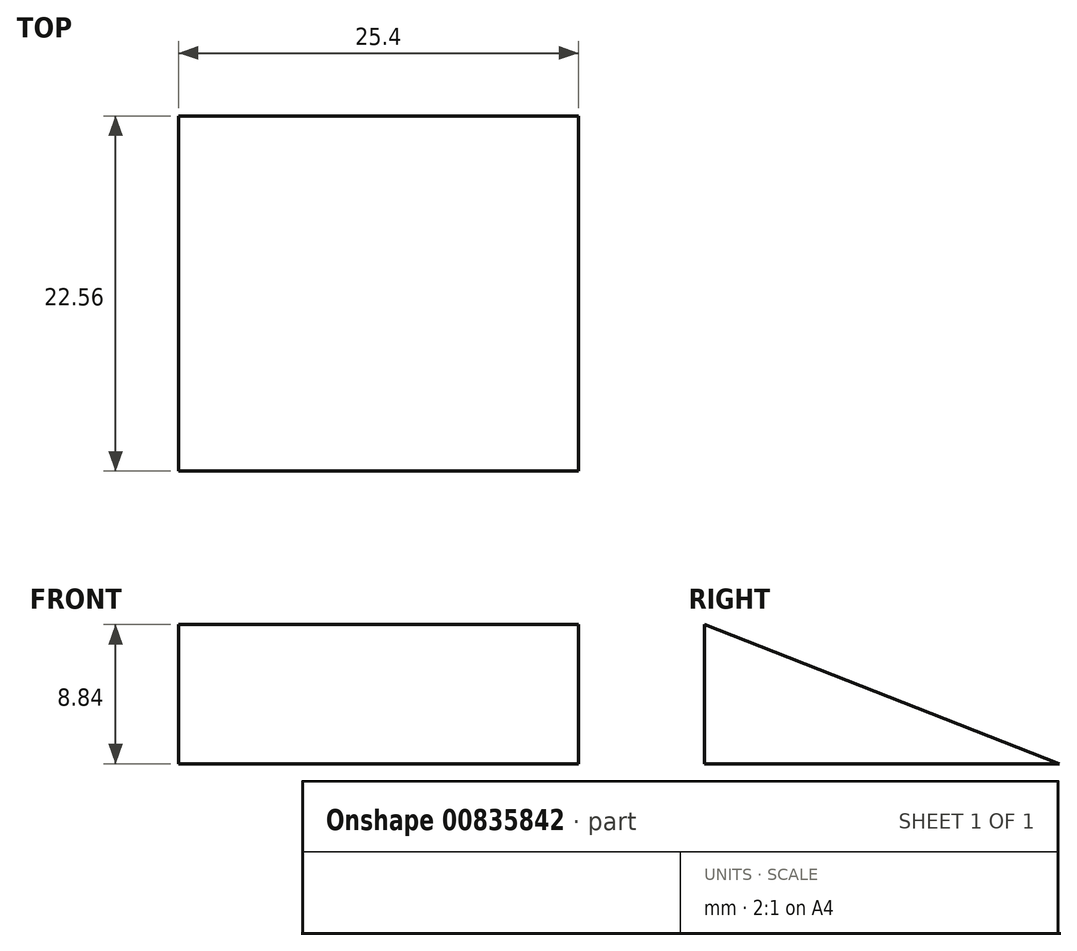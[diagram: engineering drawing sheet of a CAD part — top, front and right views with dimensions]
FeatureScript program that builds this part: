
annotation { "Feature Type Name" : "Feature", "Feature Type Description" : "" }
export const myFeature = defineFeature(function(context is Context, id is Id, definition is map)
    precondition{}
    {
        {
            var Q0;
            Q0=qCreatedBy(makeId("Right.planeOp"),FACE);
            var sketch = newSketch(context, id + "F0", { "sketchPlane" : qUnion([Q0])});
            skLineSegment(sketch, "E0", {"start": v(0, 0) * mm, "end": v(22.56, 0) * mm});
            skLineSegment(sketch, "E1", {"start": v(22.56, 0) * mm, "end": v(0, 8.84) * mm});
            skLineSegment(sketch, "E2", {"start": v(0, 8.84) * mm, "end": v(0, 0) * mm});
            skSolve(sketch);
        }
        {
            var Q0;
            Q0 = qSketchRegion(id + "F0", true);
            extrude(context, id + "F1", {"entities" : qUnion([Q0]), "depth" : 25.4 * mm, "offsetDistance" : 25.4 * mm});
        }
    });
